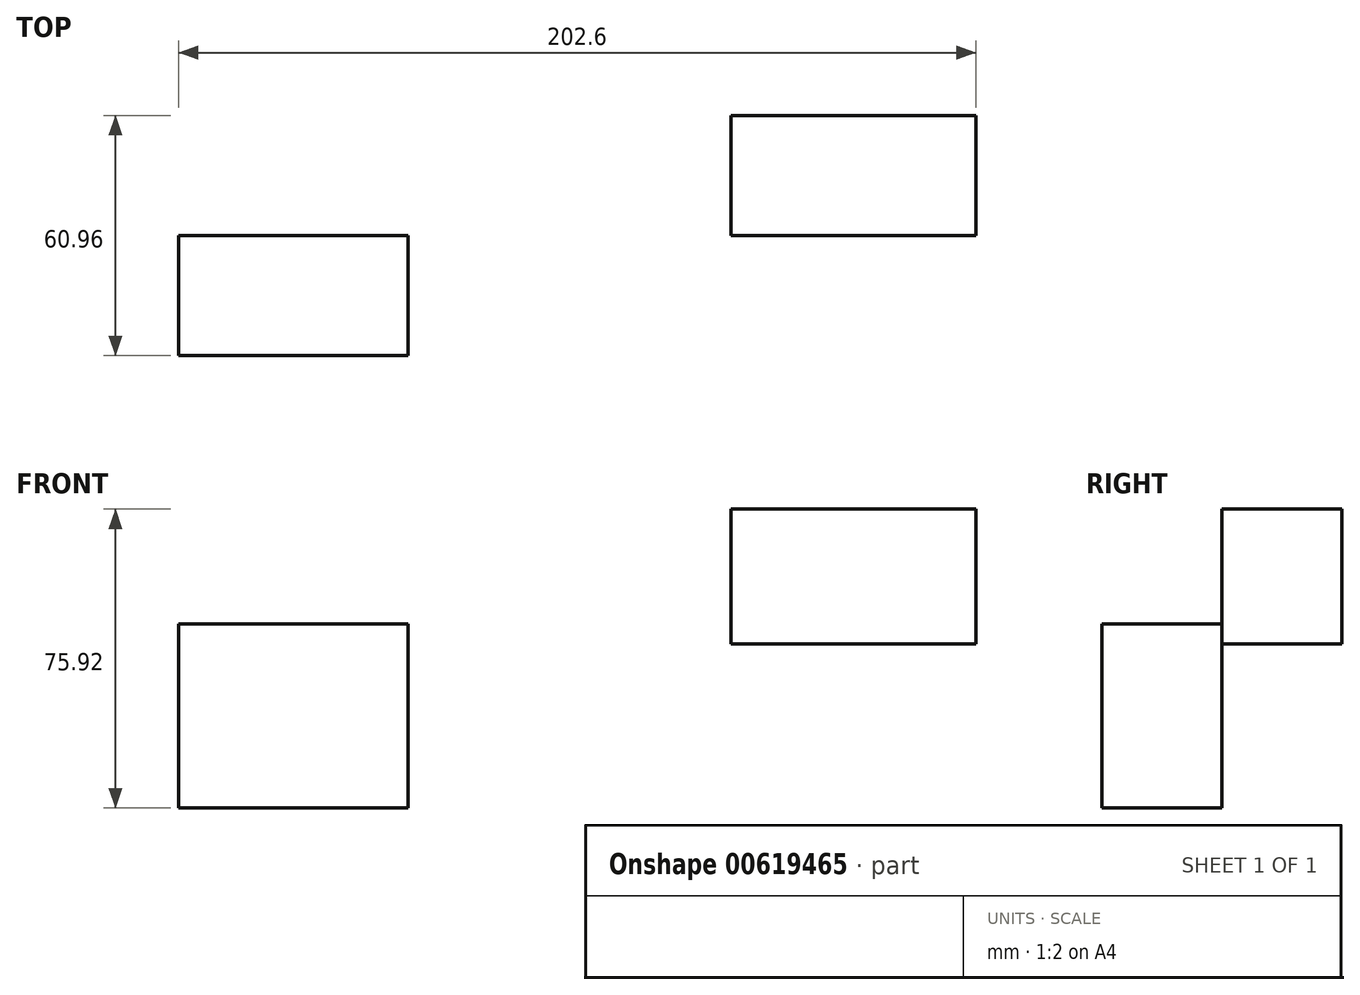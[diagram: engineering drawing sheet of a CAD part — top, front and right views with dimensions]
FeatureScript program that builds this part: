
annotation { "Feature Type Name" : "Feature", "Feature Type Description" : "" }
export const myFeature = defineFeature(function(context is Context, id is Id, definition is map)
    precondition{}
    {
        {
            var Q0;
            Q0=qCreatedBy(makeId("Front.planeOp"),FACE);
            var sketch = newSketch(context, id + "F0", { "sketchPlane" : qUnion([Q0])});
            skLineSegment(sketch, "E0.bottom", {"start": v(-137.34, 37.02) * mm, "end": v(-78.98, 37.02) * mm});
            skLineSegment(sketch, "E0.top", {"start": v(-137.34, -9.77) * mm, "end": v(-78.98, -9.77) * mm});
            skLineSegment(sketch, "E0.left", {"start": v(-137.34, 37.02) * mm, "end": v(-137.34, -9.77) * mm});
            skLineSegment(sketch, "E0.right", {"start": v(-78.98, 37.02) * mm, "end": v(-78.98, -9.77) * mm});
            skSolve(sketch);
        }
        {
            var Q0;
            Q0 = qSketchRegion(id + "F0", true);
            extrude(context, id + "F1", {"entities" : qUnion([Q0]), "depth" : 30.48 * mm, "offsetDistance" : 30.48 * mm});
        }
        {
            var Q0;
            Q0=qCreatedBy(makeId("Front.planeOp"),FACE);
            var sketch = newSketch(context, id + "F2", { "sketchPlane" : qUnion([Q0])});
            skLineSegment(sketch, "E1.bottom", {"start": v(3.1, 66.15) * mm, "end": v(65.26, 66.15) * mm});
            skLineSegment(sketch, "E1.top", {"start": v(3.1, 31.86) * mm, "end": v(65.26, 31.86) * mm});
            skLineSegment(sketch, "E1.left", {"start": v(3.1, 66.15) * mm, "end": v(3.1, 31.86) * mm});
            skLineSegment(sketch, "E1.right", {"start": v(65.26, 66.15) * mm, "end": v(65.26, 31.86) * mm});
            skSolve(sketch);
        }
        {
            var Q0;
            Q0 = qSketchRegion(id + "F2", true);
            extrude(context, id + "F3", {"entities" : qUnion([Q0]), "oppositeDirection" : true, "depth" : 30.48 * mm, "offsetDistance" : 30.48 * mm});
        }
    });
